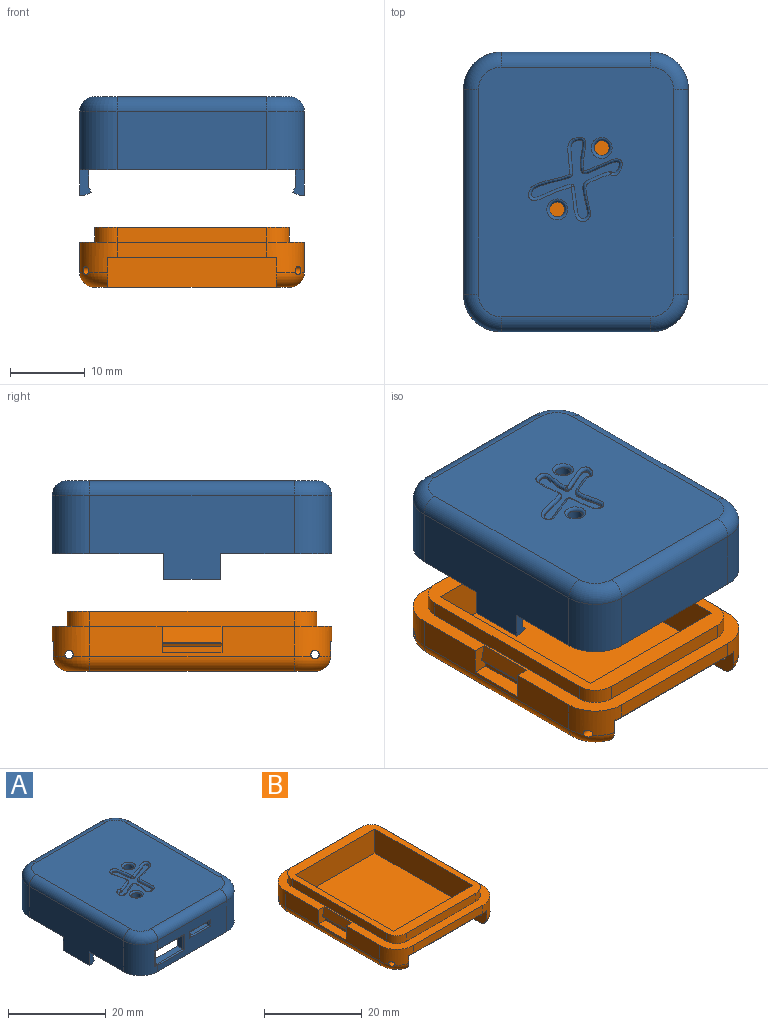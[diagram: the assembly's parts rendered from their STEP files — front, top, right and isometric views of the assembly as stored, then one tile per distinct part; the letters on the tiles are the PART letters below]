
ASSEMBLY  parts=2 mates=2
PART A: 94 faces, bbox 30.8x38.1x13.2 mm
  f0: plane 33.3x26mm, normal (0,0,1), area 802.8mm2, adj f41,f42,f43,f44,f45,f46,f47,f48
  f1: plane 31.63x6.2mm, normal (1,0,0), area 192.1mm2, adj f16,f19,f21,f40,f69,f71
  f2: plane 20x7.75mm, normal (0,-1,0), area 114.4mm2, adj f4,f10,f11,f42,f74,f76,f77,f78
  f3: plane 20x8.2mm, normal (0,1,0), area 131.1mm2, adj f4,f16,f17,f40,f62,f63,f64,f65
  f4: plane 37.3x30mm, normal (0,0,-1), area 198.4mm2, adj f2,f3,f5,f6,f7,f8,f9,f10
  f5: plane 27.3x11.15mm, normal (1,0,0), area 237.4mm2, adj f4,f8,f11,f46,f56,f59,f60
  f6: plane 20x7.75mm, normal (0,1,0), area 155mm2, adj f4,f8,f9,f47
  f7: plane 27.3x11.15mm, normal (-1,0,0), area 237.4mm2, adj f4,f9,f10,f43,f49,f53,f54
  f8: cylinder r=5mm len=7.75mm, axis (0,0,-1), area 60.9mm2, adj f4,f5,f6,f48
  f9: cylinder r=5mm len=7.75mm, axis (0,0,1), area 60.9mm2, adj f4,f6,f7,f45
  f10: cylinder r=5mm len=7.75mm, axis (0,0,-1), area 57.7mm2, adj f2,f4,f7,f41,f72,f73,f75
  f11: cylinder r=5mm len=7.75mm, axis (0,0,1), area 60.9mm2, adj f2,f4,f5,f44
  f12: cylinder r=3.2mm len=3.2mm, axis (0,0,1), area 10.1mm2, adj f4,f13,f18,f19
  f13: plane 20x2mm, normal (0,-1,0), area 40mm2, adj f4,f12,f14,f19
  f14: cylinder r=3.2mm len=3.2mm, axis (0,0,1), area 10.1mm2, adj f4,f13,f15,f19
  f15: plane 27.3x2mm, normal (1,0,0), area 54.6mm2, adj f4,f14,f16,f19
  f16: cylinder r=3.2mm len=7.1mm, axis (0,0,1), area 16.3mm2, adj f1,f3,f4,f15,f19,f61,f62,f64
  f17: cylinder r=3.2mm len=8.2mm, axis (0,0,1), area 19.7mm2, adj f3,f4,f18,f19,f20,f40
  f18: plane 27.3x2mm, normal (-1,0,0), area 54.6mm2, adj f4,f12,f17,f19
  f19: plane 33.33x26.4mm, normal (0,0,-1), area 195.2mm2, adj f1,f12,f13,f14,f15,f16,f17,f18
  f20: plane 14.43x6.2mm, normal (-1,0,0), area 89.4mm2, adj f17,f19,f39,f40
  f21: plane 18x6.2mm, normal (0,-1,0), area 111.6mm2, adj f1,f19,f22,f40
  f22: plane 6.2x2.15mm, normal (-1,0,0), area 13.3mm2, adj f19,f21,f23,f40
  f23: plane 6.2x5mm, normal (0,-1,0), area 31mm2, adj f19,f22,f24,f40
  f24: plane 6.2x1.65mm, normal (-1,0,0), area 10.2mm2, adj f19,f23,f25,f40
  f25: plane 6.2x5.03mm, normal (0,1,0), area 31.2mm2, adj f19,f24,f26,f40
  f26: plane 6.2x1.35mm, normal (-1,0,0), area 8.4mm2, adj f19,f25,f27,f40
  f27: plane 6.2x5mm, normal (0,-1,0), area 31mm2, adj f19,f26,f28,f40
  f28: plane 6.2x1.77mm, normal (-1,0,0), area 11mm2, adj f19,f27,f29,f40
  f29: plane 6.2x4.99mm, normal (0,1,0), area 30.9mm2, adj f19,f28,f30,f40
  f30: plane 6.2x2.2mm, normal (-1,0,0), area 13.6mm2, adj f19,f29,f31,f40
  f31: plane 6.2x5mm, normal (0,-1,0), area 31mm2, adj f19,f30,f32,f40
  f32: plane 6.2x1.83mm, normal (-1,0,0), area 11.3mm2, adj f19,f31,f33,f40
  f33: plane 6.2x4.98mm, normal (0,1,0), area 30.9mm2, adj f19,f32,f34,f40
  f34: plane 6.2x2.2mm, normal (-1,0,0), area 13.6mm2, adj f19,f33,f35,f40
  f35: plane 6.2x5mm, normal (0,-1,0), area 31mm2, adj f19,f34,f36,f40
  f36: plane 6.2x2mm, normal (-1,0,0), area 12.4mm2, adj f19,f35,f37,f40
  f37: plane 6.2x5mm, normal (0,1,0), area 31mm2, adj f19,f36,f38,f40
  f38: plane 6.2x2.05mm, normal (-1,0,0), area 12.7mm2, adj f19,f37,f39,f40
  f39: plane 6.2x5mm, normal (0,-1,0), area 31mm2, adj f19,f20,f38,f40
  f40: plane 32x23mm, normal (0,0,-1), area 671.6mm2, adj f1,f3,f17,f20,f21,f22,f23,f24
  f41: torus R=3mm, axis (0,0,1), area 21.1mm2, adj f0,f10,f42,f43
  f42: cylinder r=2mm len=20mm, axis (1,0,0), area 62.8mm2, adj f0,f2,f41,f44
  f43: cylinder r=2mm len=27.3mm, axis (0,-1,0), area 85.8mm2, adj f0,f7,f41,f45
  f44: torus R=3mm, axis (0,0,1), area 21.1mm2, adj f0,f11,f42,f46
  f45: torus R=3mm, axis (0,0,1), area 21.1mm2, adj f0,f9,f43,f47
  f46: cylinder r=2mm len=27.3mm, axis (0,1,0), area 85.8mm2, adj f0,f5,f44,f48
  f47: cylinder r=2mm len=20mm, axis (-1,0,0), area 62.8mm2, adj f0,f6,f45,f48
  f48: torus R=3mm, axis (0,0,1), area 21.1mm2, adj f0,f8,f46,f47
  f49: plane 7.6x0.7mm, normal (0,0,-1), area 5.3mm2, adj f7,f50,f53,f54
  f50: plane 7.6x0.9mm, normal (0.41,0,-0.91), area 7.5mm2, adj f49,f51,f53,f54
  f51: plane 7.6x0.6mm, normal (0.83,0,0.55), area 5.5mm2, adj f50,f52,f53,f54
  f52: plane 7.6x2.4mm, normal (1,0,0), area 18.2mm2, adj f4,f51,f53,f54
  f53: plane 3.4x1.6mm, normal (0,-1,0), area 4.2mm2, adj f4,f7,f49,f50,f51,f52
  f54: plane 3.4x1.6mm, normal (0,1,0), area 4.2mm2, adj f4,f7,f49,f50,f51,f52
  f55: plane 7.6x0.9mm, normal (-0.41,0,-0.91), area 7.5mm2, adj f56,f58,f59,f60
  f56: plane 7.6x0.7mm, normal (0,0,-1), area 5.3mm2, adj f5,f55,f59,f60
  f57: plane 7.6x2.4mm, normal (-1,0,0), area 18.2mm2, adj f4,f58,f59,f60
  f58: plane 7.6x0.6mm, normal (-0.83,0,0.55), area 5.5mm2, adj f55,f57,f59,f60
  f59: plane 3.4x1.6mm, normal (0,-1,0), area 4.2mm2, adj f4,f5,f55,f56,f57,f58
  f60: plane 3.4x1.6mm, normal (0,1,0), area 4.2mm2, adj f4,f5,f55,f56,f57,f58
  f61: plane 3.5x1.53mm, normal (1,0,0), area 5.4mm2, adj f16,f62,f64,f73
  f62: plane 8x1.59mm, normal (0,0,1), area 12.4mm2, adj f3,f16,f61,f63,f72,f73,f74
  f63: plane 3.5x1.55mm, normal (-1,0,0), area 5.4mm2, adj f3,f62,f64,f76
  f64: plane 8x1.59mm, normal (0,0,-1), area 12.4mm2, adj f3,f16,f61,f63,f73,f75,f77
  f65: plane 5.5x1.55mm, normal (0,0,-1), area 8.5mm2, adj f3,f66,f68,f78
  f66: plane 1.55x1.1mm, normal (1,0,0), area 1.7mm2, adj f3,f65,f67,f79
  f67: plane 5.5x1.55mm, normal (0,0,1), area 8.5mm2, adj f3,f66,f68,f81
  f68: plane 1.55x1.1mm, normal (-1,0,0), area 1.7mm2, adj f3,f65,f67,f80
  f69: plane 2x1.1mm, normal (0,1,0), area 2.2mm2, adj f1,f40,f70,f71
  f70: plane 4x1.1mm, normal (1,0,0), area 4.4mm2, adj f3,f40,f69,f71
  f71: plane 4x2mm, normal (0,0,-1), area 7.8mm2, adj f1,f3,f16,f69,f70
  f72: torus R=4.75mm, axis (0,0,-1), area 0.3mm2, adj f10,f62,f73,f74
  f73: cylinder r=0.25mm len=4mm, axis (0,0,-1), area 1.6mm2, adj f10,f61,f62,f64,f72,f75
  f74: cylinder r=0.25mm len=7.75mm, axis (1,0,0), area 3mm2, adj f2,f62,f72,f76
  f75: torus R=4.75mm, axis (0,0,-1), area 0.3mm2, adj f10,f64,f73,f77
  f76: cylinder r=0.25mm len=4mm, axis (0,0,1), area 1.5mm2, adj f2,f63,f74,f77
  f77: cylinder r=0.25mm len=7.75mm, axis (-1,0,0), area 3mm2, adj f2,f64,f75,f76
  f78: cylinder r=0.25mm len=6mm, axis (-1,0,0), area 2.3mm2, adj f2,f65,f79,f80
  f79: cylinder r=0.25mm len=1.6mm, axis (0,0,-1), area 0.5mm2, adj f2,f66,f78,f81
  f80: cylinder r=0.25mm len=1.6mm, axis (0,0,1), area 0.5mm2, adj f2,f68,f78,f81
  f81: cylinder r=0.25mm len=6mm, axis (1,0,0), area 2.3mm2, adj f2,f67,f79,f80
  f82: cylinder r=1mm len=2mm, axis (0,0,1), area 7.2mm2, adj f40,f93
  f83: cylinder r=1mm len=2mm, axis (0,0,-1), area 7.2mm2, adj f40,f92
  f84: extruded ~11.65x10.25mm, area 6.4mm2, adj f85,f86,f87,f88,f89,f90,f91
  f85: plane 11.85x10.61mm, normal (0,0,1), area 23.9mm2, adj f84
  f86: bspline ~5.36x2.26mm, area 4.7mm2, adj f0,f84,f87,f88
  f87: bspline ~0.4x0.4mm, area 0mm2, adj f84,f86,f89
  f88: bspline ~0.4x0.38mm, area 0.1mm2, adj f84,f86,f90
  f89: bspline ~6.65x5.42mm, area 8.8mm2, adj f0,f84,f87,f91
  f90: bspline ~8.46x7.68mm, area 14.2mm2, adj f0,f84,f88,f91
  f91: bspline ~0.4x0.4mm, area 0.1mm2, adj f84,f89,f90
  f92: torus R=1.4mm, axis (0,0,1), area 4.5mm2, adj f0,f83
  f93: torus R=1.4mm, axis (0,0,1), area 4.5mm2, adj f0,f82
PART B: 58 faces, bbox 30.8x37.8x8 mm
  f0: cylinder r=5mm len=5mm, axis (0,0,1), area 28mm2, adj f3,f4,f6,f7,f30,f33,f54
  f1: cylinder r=5mm len=5mm, axis (0,0,-1), area 28mm2, adj f2,f5,f6,f7,f32,f33,f56
  f2: torus R=3mm, axis (0,0,1), area 16.8mm2, adj f1,f11,f32,f35,f56
  f3: torus R=3mm, axis (0,0,1), area 16.8mm2, adj f0,f11,f30,f37,f54
  f4: plane 27.3x4mm, normal (1,0,0), area 81.2mm2, adj f0,f6,f9,f37,f40,f42,f43
  f5: plane 27.3x4mm, normal (-1,0,0), area 81.2mm2, adj f1,f6,f12,f35,f45,f48,f49
  f6: plane 37.3x30mm, normal (0,0,1), area 213mm2, adj f0,f1,f4,f5,f7,f8,f9,f12
  f7: plane 20x2mm, normal (0,1,0), area 40mm2, adj f0,f1,f6,f33
  f8: plane 20x2mm, normal (0,-1,0), area 40mm2, adj f6,f9,f12,f29
  f9: cylinder r=5mm len=5mm, axis (0,0,-1), area 28mm2, adj f4,f6,f8,f27,f29,f36,f55
  f10: plane 33.3x26mm, normal (0,0,1), area 207.2mm2, adj f13,f14,f15,f16,f17,f18,f19,f20
  f11: plane 32.75x26mm, normal (0,0,-1), area 768.4mm2, adj f2,f3,f26,f27,f28,f30,f31,f32
  f12: cylinder r=5mm len=5mm, axis (0,0,1), area 28mm2, adj f5,f6,f8,f28,f29,f34,f57
  f13: cylinder r=3mm len=3mm, axis (0,0,1), area 9.4mm2, adj f6,f10,f14,f20
  f14: plane 27.3x2mm, normal (1,0,0), area 54.6mm2, adj f6,f10,f13,f15
  f15: cylinder r=3mm len=3mm, axis (0,0,1), area 9.4mm2, adj f6,f10,f14,f16
  f16: plane 20x2mm, normal (0,-1,0), area 40mm2, adj f6,f10,f15,f17
  f17: cylinder r=3mm len=3mm, axis (0,0,1), area 9.4mm2, adj f6,f10,f16,f18
  f18: plane 27.3x2mm, normal (-1,0,0), area 54.6mm2, adj f6,f10,f17,f19
  f19: cylinder r=3mm len=3mm, axis (0,0,1), area 9.4mm2, adj f6,f10,f18,f20
  f20: plane 20x2mm, normal (0,1,0), area 40mm2, adj f6,f10,f13,f19
  f21: plane 28.3x6mm, normal (1,0,0), area 169.8mm2, adj f10,f22,f24,f25
  f22: plane 23x6mm, normal (0,1,0), area 138mm2, adj f10,f21,f23,f25
  f23: plane 28.3x6mm, normal (-1,0,0), area 169.8mm2, adj f10,f22,f24,f25
  f24: plane 23x6mm, normal (0,-1,0), area 138mm2, adj f10,f21,f23,f25
  f25: plane 28.3x23mm, normal (0,0,1), area 650.8mm2, adj f21,f22,f23,f24
  f26: plane 22.5x4mm, normal (0,-1,0), area 90mm2, adj f11,f27,f28,f29
  f27: plane 4x3.84mm, normal (-1,0,0), area 13.5mm2, adj f9,f11,f26,f29,f36,f55
  f28: plane 4x3.84mm, normal (1,0,0), area 13.5mm2, adj f11,f12,f26,f29,f34,f57
  f29: plane 22.5x4mm, normal (0,0,-1), area 89.9mm2, adj f8,f9,f12,f26,f27,f28
  f30: plane 4x3.84mm, normal (-1,0,0), area 13.5mm2, adj f0,f3,f11,f31,f33,f54
  f31: plane 22.5x4mm, normal (0,1,0), area 90mm2, adj f11,f30,f32,f33
  f32: plane 4x3.84mm, normal (1,0,0), area 13.5mm2, adj f1,f2,f11,f31,f33,f56
  f33: plane 22.5x4mm, normal (0,0,-1), area 89.9mm2, adj f0,f1,f7,f30,f31,f32
  f34: torus R=3mm, axis (0,0,1), area 16.8mm2, adj f11,f12,f28,f35,f57
  f35: cylinder r=2mm len=27.3mm, axis (0,-1,0), area 85.8mm2, adj f2,f5,f11,f34
  f36: torus R=3mm, axis (0,0,1), area 16.8mm2, adj f9,f11,f27,f37,f55
  f37: cylinder r=2mm len=27.3mm, axis (0,1,0), area 85.8mm2, adj f3,f4,f11,f36
  f38: plane 8x0.47mm, normal (0.26,0,-0.97), area 3.9mm2, adj f42,f43,f50,f51
  f39: plane 8x0.85mm, normal (1,0,0), area 6.8mm2, adj f40,f42,f43,f50
  f40: plane 8x2mm, normal (0,0,1), area 16mm2, adj f4,f39,f42,f43
  f41: plane 8x2.1mm, normal (0.98,0,0.2), area 17.1mm2, adj f6,f42,f43,f51
  f42: plane 3.5x2mm, normal (0,-1,0), area 5.6mm2, adj f4,f6,f38,f39,f40,f41,f50,f51
  f43: plane 3.5x2mm, normal (0,1,0), area 5.6mm2, adj f4,f6,f38,f39,f40,f41,f50,f51
  f44: plane 8x2.1mm, normal (-0.98,0,0.2), area 17.1mm2, adj f6,f48,f49,f53
  f45: plane 8x2mm, normal (0,0,1), area 16mm2, adj f5,f46,f48,f49
  f46: plane 8x0.85mm, normal (-1,0,0), area 6.8mm2, adj f45,f48,f49,f52
  f47: plane 8x0.47mm, normal (-0.26,0,-0.97), area 3.9mm2, adj f48,f49,f52,f53
  f48: plane 3.5x2mm, normal (0,-1,0), area 5.6mm2, adj f5,f6,f44,f45,f46,f47,f52,f53
  f49: plane 3.5x2mm, normal (0,1,0), area 5.6mm2, adj f5,f6,f44,f45,f46,f47,f52,f53
  f50: cylinder r=0.2mm len=8mm, axis (0,1,0), area 2.1mm2, adj f38,f39,f42,f43
  f51: cylinder r=0.2mm len=8mm, axis (0,-1,0), area 2.4mm2, adj f38,f41,f42,f43
  f52: cylinder r=0.2mm len=8mm, axis (0,1,0), area 2.1mm2, adj f46,f47,f48,f49
  f53: cylinder r=0.2mm len=8mm, axis (0,-1,0), area 2.4mm2, adj f44,f47,f48,f49
  f54: cylinder r=0.55mm len=3.24mm, axis (1,0,0), area 10mm2, adj f0,f3,f30
  f55: cylinder r=0.55mm len=3.24mm, axis (1,0,0), area 10mm2, adj f9,f27,f36
  f56: cylinder r=0.55mm len=3.24mm, axis (1,0,0), area 10mm2, adj f1,f2,f32
  f57: cylinder r=0.55mm len=3.24mm, axis (1,0,0), area 10mm2, adj f12,f28,f34
PLACE A rot(axis=(0,0,1),180deg) t=(-11.27,7.47,26.26)mm
PLACE B t=(-11.27,7.47,0.81)mm fixed
MATE parallel A.f6 <-> B.f8  axis (0,-1,0) through (-11.27,-11.18,20.38)mm
MATE parallel A.f7 <-> B.f4  axis (1,0,0) through (3.73,7.47,19.77)mm
